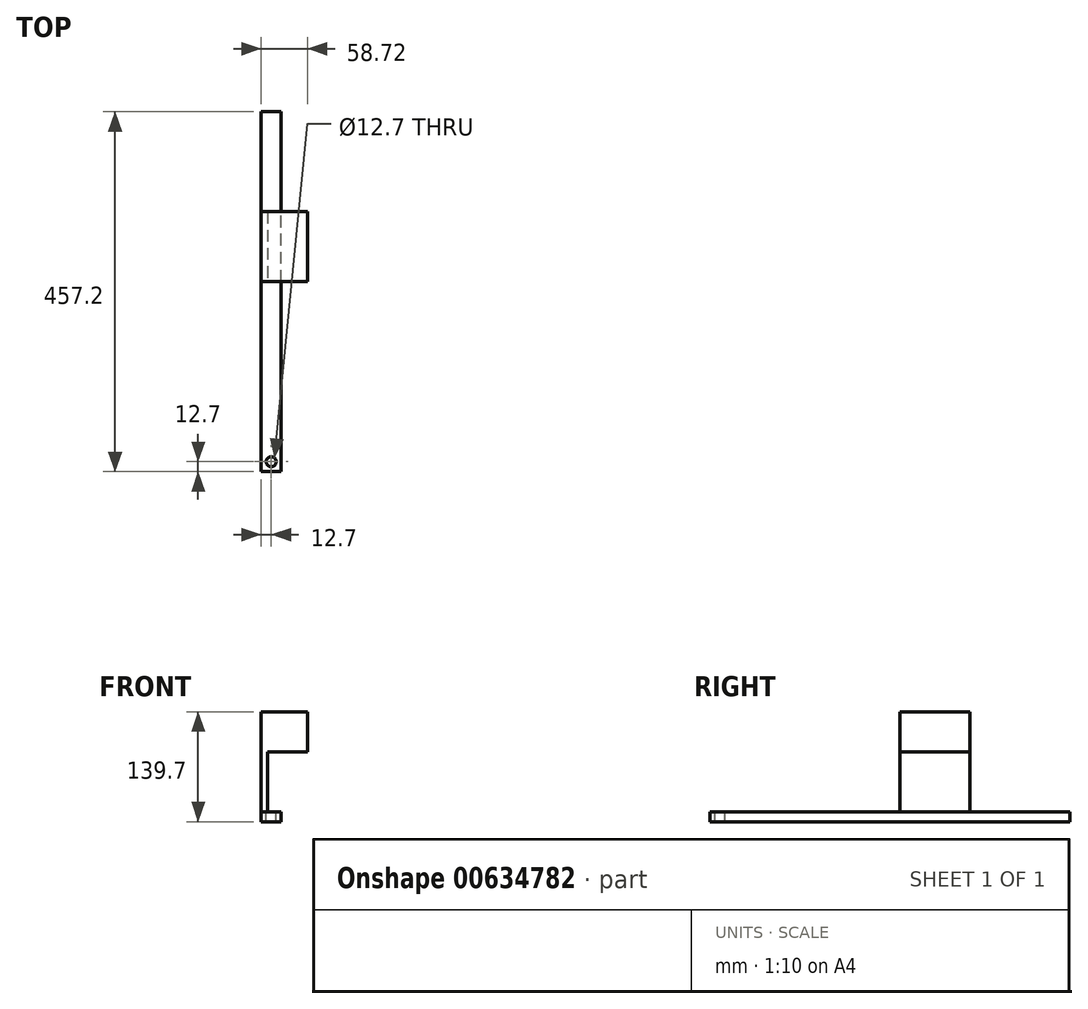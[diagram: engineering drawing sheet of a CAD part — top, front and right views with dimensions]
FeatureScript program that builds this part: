
annotation { "Feature Type Name" : "Feature", "Feature Type Description" : "" }
export const myFeature = defineFeature(function(context is Context, id is Id, definition is map)
    precondition{}
    {
        {
            var Q0;
            Q0=qCreatedBy(makeId("Front.planeOp"),FACE);
            var sketch = newSketch(context, id + "F0", { "sketchPlane" : qUnion([Q0])});
            skLineSegment(sketch, "E0.bottom", {"start": v(12.7, 6.35) * mm, "end": v(-12.7, 6.35) * mm});
            skLineSegment(sketch, "E0.top", {"start": v(12.7, -6.35) * mm, "end": v(-12.7, -6.35) * mm});
            skLineSegment(sketch, "E0.left", {"start": v(12.7, 6.35) * mm, "end": v(12.7, -6.35) * mm});
            skLineSegment(sketch, "E0.right", {"start": v(-12.7, 6.35) * mm, "end": v(-12.7, -6.35) * mm});
            skPoint(sketch, "E0.middle", {"position": v(0, 0) * mm});
            skSolve(sketch);
        }
        {
            var Q0;
            Q0 = qSketchRegion(id + "F0", true);
            extrude(context, id + "F1", {"entities" : qUnion([Q0]), "depth" : 457.2 * mm, "offsetDistance" : 25.4 * mm});
        }
        {
            var Q0;
            Q0=makeQuery(id+"F1.opExtrude","SWEPT_FACE",FACE,{"disambiguationData":[OSD([sQuery(id+"F0.wireOp",EDGE,"E0.bottom")])]});
            var sketch = newSketch(context, id + "F2", { "sketchPlane" : qUnion([Q0])});
            skLineSegment(sketch, "E1.bottom", {"start": v(-12.7, -127) * mm, "end": v(-4.78, -127) * mm});
            skLineSegment(sketch, "E1.top", {"start": v(-12.7, -215.9) * mm, "end": v(-4.78, -215.9) * mm});
            skLineSegment(sketch, "E1.left", {"start": v(-12.7, -127) * mm, "end": v(-12.7, -215.9) * mm});
            skLineSegment(sketch, "E1.right", {"start": v(-4.78, -127) * mm, "end": v(-4.78, -215.9) * mm});
            skSolve(sketch);
        }
        {
            var Q0;
            Q0 = qSketchRegion(id + "F2", true);
            extrude(context, id + "F3", {"entities" : qUnion([Q0]), "operationType" : NewBodyOperationType.ADD, "depth" : 127 * mm, "offsetDistance" : 25.4 * mm});
        }
        {
            var Q0;
            Q0=makeQuery(id+"F3.opExtrude","SWEPT_FACE",FACE,{"disambiguationData":[OSD([sQuery(id+"F2.wireOp",EDGE,"E1.right")])]});
            var sketch = newSketch(context, id + "F4", { "sketchPlane" : qUnion([Q0])});
            skLineSegment(sketch, "E2.bottom", {"start": v(-215.9, 133.35) * mm, "end": v(-127, 133.35) * mm});
            skLineSegment(sketch, "E2.top", {"start": v(-215.9, 82.55) * mm, "end": v(-127, 82.55) * mm});
            skLineSegment(sketch, "E2.left", {"start": v(-215.9, 133.35) * mm, "end": v(-215.9, 82.55) * mm});
            skLineSegment(sketch, "E2.right", {"start": v(-127, 133.35) * mm, "end": v(-127, 82.55) * mm});
            skSolve(sketch);
        }
        {
            var Q0;
            Q0 = qSketchRegion(id + "F4", true);
            extrude(context, id + "F5", {"entities" : qUnion([Q0]), "operationType" : NewBodyOperationType.ADD, "depth" : 50.8 * mm, "offsetDistance" : 25.4 * mm});
        }
        {
            var Q0;
            Q0=makeQuery(id+"F1.opExtrude","SWEPT_FACE",FACE,{"disambiguationData":[OSD([sQuery(id+"F0.wireOp",EDGE,"E0.bottom")])]});
            var sketch = newSketch(context, id + "F6", { "sketchPlane" : qUnion([Q0])});
            skCircle(sketch, "E3", {"center": v(0, -444.5) * mm, "radius": 6.35 * mm});
            skPoint(sketch, "E3.centerSnap0", {"position": v(0, -457.2) * mm});
            skSolve(sketch);
        }
        {
            var Q0;
            Q0 = qSketchRegion(id + "F6", true);
            extrude(context, id + "F7", {"entities" : qUnion([Q0]), "operationType" : NewBodyOperationType.REMOVE, "oppositeDirection" : true, "depth" : 25.4 * mm, "offsetDistance" : 25.4 * mm});
        }
    });
